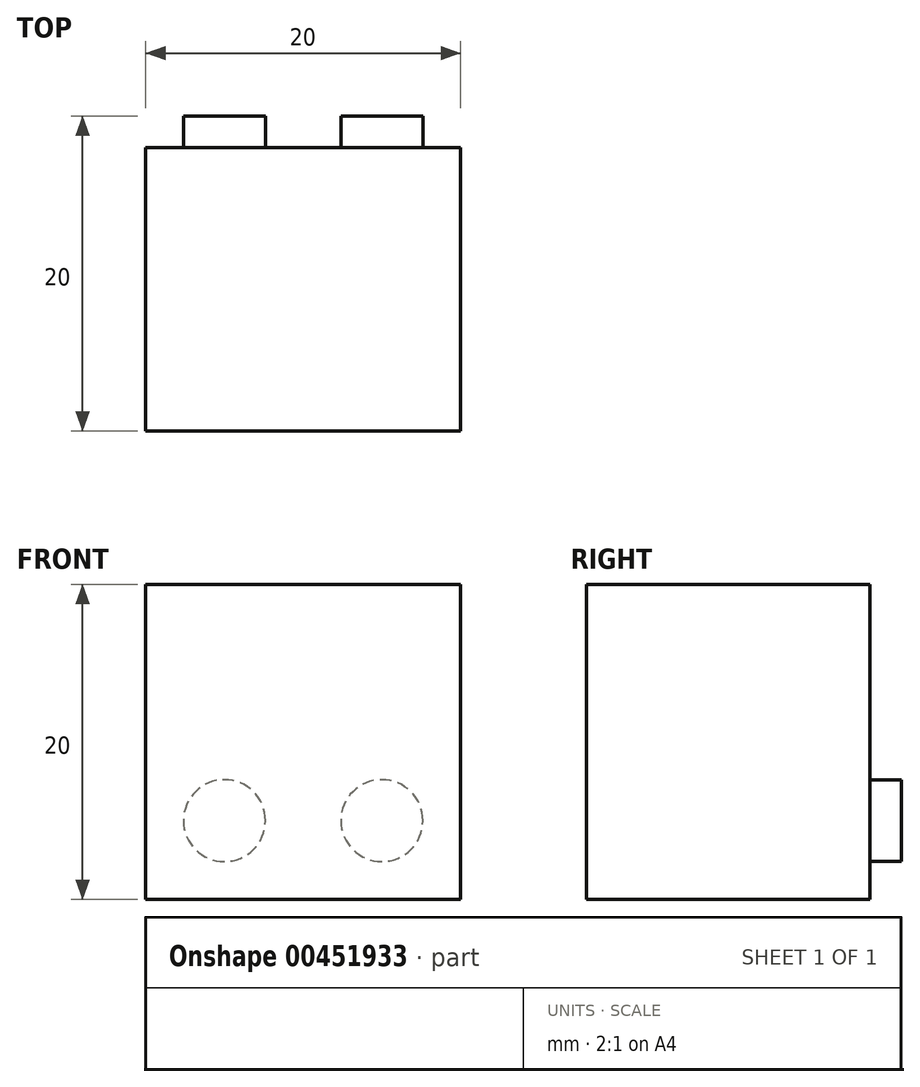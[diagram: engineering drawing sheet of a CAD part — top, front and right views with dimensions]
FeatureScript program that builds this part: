
annotation { "Feature Type Name" : "Feature", "Feature Type Description" : "" }
export const myFeature = defineFeature(function(context is Context, id is Id, definition is map)
    precondition{}
    {
        {
            var Q0;
            Q0=qCreatedBy(makeId("Front.planeOp"),FACE);
            var sketch = newSketch(context, id + "F0", { "sketchPlane" : qUnion([Q0])});
            skLineSegment(sketch, "E0.bottom", {"start": v(0, 0) * mm, "end": v(20, 0) * mm});
            skLineSegment(sketch, "E0.top", {"start": v(0, 20) * mm, "end": v(20, 20) * mm});
            skLineSegment(sketch, "E0.left", {"start": v(0, 0) * mm, "end": v(0, 20) * mm});
            skLineSegment(sketch, "E0.right", {"start": v(20, 0) * mm, "end": v(20, 20) * mm});
            skSolve(sketch);
        }
        {
            var Q0;
            Q0 = qSketchRegion(id + "F0", true);
            extrude(context, id + "F1", {"entities" : qUnion([Q0]), "depth" : 20 * mm});
        }
        {
            var Q0;
            Q0=makeQuery(id+"F1.opExtrude","CAP_FACE",FACE,{"disambiguationData":[OSD([sQuery(id+"F0.wireOp",EDGE,"E0.bottom"),sQuery(id+"F0.wireOp",EDGE,"E0.top"),sQuery(id+"F0.wireOp",EDGE,"E0.left"),sQuery(id+"F0.wireOp",EDGE,"E0.right")])],"isStart":true});
            var sketch = newSketch(context, id + "F2", { "sketchPlane" : qUnion([Q0])});
            skLineSegment(sketch, "E1", {"start": v(-20, 20) * mm, "end": v(0, 0) * mm, "construction": true});
            skLineSegment(sketch, "E2", {"start": v(0, 20) * mm, "end": v(-20, 0) * mm, "construction": true});
            skLineSegment(sketch, "E3", {"start": v(-10, 20) * mm, "end": v(-10, 0) * mm, "construction": true});
            skLineSegment(sketch, "E4", {"start": v(-20, 10) * mm, "end": v(0.43, 10) * mm, "construction": true});
            skCircle(sketch, "E5", {"center": v(-10, 10) * mm, "radius": 2.6 * mm});
            skCircle(sketch, "E6", {"center": v(-15, 15) * mm, "radius": 2.6 * mm});
            skCircle(sketch, "E7.MirrorC", {"center": v(-15, 5) * mm, "radius": 2.6 * mm});
            skLineSegment(sketch, "E8.MirrorCS", {"start": v(-20, 0) * mm, "end": v(0, 20) * mm, "construction": true});
            skCircle(sketch, "E9.MirrorC", {"center": v(-5, 15) * mm, "radius": 2.6 * mm});
            skCircle(sketch, "E10.MirrorC", {"center": v(-5, 5) * mm, "radius": 2.6 * mm});
            skSolve(sketch);
        }
        {
            var Q0;
            Q0=makeQuery(id+"F2.imprint","IMPRINT",FACE,{"disambiguationData":[TD([[makeQuery(id+"F2.imprint","IMPRINT",EDGE,{"derivedFrom":sQuery(id+"F2.wireOp",EDGE,"E5")}),-1.0]])]});
            var sketch = newSketch(context, id + "F3", { "sketchPlane" : qUnion([Q0])});
            skSolve(sketch);
        }
        {
            var Q0;
            Q0=makeQuery(id+"F3.imprint","IMPRINT",FACE,{"disambiguationData":[TD([[makeQuery(id+"F3.imprint","IMPRINT",EDGE,{"derivedFrom":makeQuery(id+"F2.imprint","IMPRINT",EDGE,{"derivedFrom":sQuery(id+"F2.wireOp",EDGE,"E7.MirrorC")})}),-1.0]])]});
            var sketch = newSketch(context, id + "F4", { "sketchPlane" : qUnion([Q0])});
            skSolve(sketch);
        }
        {
            var Q0;
            Q0=makeQuery(id+"F3.imprint","IMPRINT",FACE,{"disambiguationData":[TD([[makeQuery(id+"F3.imprint","IMPRINT",EDGE,{"derivedFrom":makeQuery(id+"F2.imprint","IMPRINT",EDGE,{"derivedFrom":sQuery(id+"F2.wireOp",EDGE,"E5")})}),-1.0]])]});
            var sketch = newSketch(context, id + "F5", { "sketchPlane" : qUnion([Q0])});
            skSolve(sketch);
        }
        {
            var Q0;
            Q0=makeQuery(id+"F3.imprint","IMPRINT",FACE,{"disambiguationData":[TD([[makeQuery(id+"F3.imprint","IMPRINT",EDGE,{"derivedFrom":makeQuery(id+"F2.imprint","IMPRINT",EDGE,{"derivedFrom":sQuery(id+"F2.wireOp",EDGE,"E5")})}),-1.0]])]});
            var Q1;
            Q1=makeQuery(id+"F3.imprint","IMPRINT",FACE,{"disambiguationData":[TD([[makeQuery(id+"F3.imprint","IMPRINT",EDGE,{"derivedFrom":makeQuery(id+"F2.imprint","IMPRINT",EDGE,{"derivedFrom":sQuery(id+"F2.wireOp",EDGE,"E9.MirrorC")})}),1.0]])]});
            extrude(context, id + "F6", {"entities" : qUnion([Q0, Q1]), "operationType" : NewBodyOperationType.REMOVE, "oppositeDirection" : true, "depth" : 1 * mm});
        }
        {
            var Q0;
            Q0=makeQuery(id+"F5.imprint","IMPRINT",FACE,{"disambiguationData":[TD([[makeQuery(id+"F5.imprint","IMPRINT",EDGE,{"derivedFrom":makeQuery(id+"F3.imprint","IMPRINT",EDGE,{"derivedFrom":makeQuery(id+"F2.imprint","IMPRINT",EDGE,{"derivedFrom":sQuery(id+"F2.wireOp",EDGE,"E5")})})}),-1.0]])]});
            var sketch = newSketch(context, id + "F7", { "sketchPlane" : qUnion([Q0])});
            skSolve(sketch);
        }
        {
            var Q0;
            Q0=makeQuery(id+"F5.imprint","IMPRINT",FACE,{"disambiguationData":[TD([[makeQuery(id+"F5.imprint","IMPRINT",EDGE,{"derivedFrom":makeQuery(id+"F3.imprint","IMPRINT",EDGE,{"derivedFrom":makeQuery(id+"F2.imprint","IMPRINT",EDGE,{"derivedFrom":sQuery(id+"F2.wireOp",EDGE,"E6")})})}),1.0]])]});
            var Q1;
            Q1=makeQuery(id+"F5.imprint","IMPRINT",FACE,{"disambiguationData":[TD([[makeQuery(id+"F5.imprint","IMPRINT",EDGE,{"derivedFrom":makeQuery(id+"F3.imprint","IMPRINT",EDGE,{"derivedFrom":makeQuery(id+"F2.imprint","IMPRINT",EDGE,{"derivedFrom":sQuery(id+"F2.wireOp",EDGE,"E9.MirrorC")})})}),1.0]])]});
            var Q2;
            Q2=makeQuery(id+"F5.imprint","IMPRINT",FACE,{"disambiguationData":[TD([[makeQuery(id+"F5.imprint","IMPRINT",EDGE,{"derivedFrom":makeQuery(id+"F3.imprint","IMPRINT",EDGE,{"derivedFrom":makeQuery(id+"F2.imprint","IMPRINT",EDGE,{"derivedFrom":sQuery(id+"F2.wireOp",EDGE,"E5")})})}),1.0]])]});
            var Q3;
            Q3=makeQuery(id+"F5.imprint","IMPRINT",FACE,{"disambiguationData":[TD([[makeQuery(id+"F5.imprint","IMPRINT",EDGE,{"derivedFrom":makeQuery(id+"F3.imprint","IMPRINT",EDGE,{"derivedFrom":makeQuery(id+"F2.imprint","IMPRINT",EDGE,{"derivedFrom":sQuery(id+"F2.wireOp",EDGE,"E10.MirrorC")})})}),-1.0]])]});
            var Q4;
            Q4=makeQuery(id+"F4.imprint","IMPRINT",FACE,{"disambiguationData":[TD([[makeQuery(id+"F4.imprint","IMPRINT",EDGE,{"derivedFrom":makeQuery(id+"F3.imprint","IMPRINT",EDGE,{"derivedFrom":makeQuery(id+"F2.imprint","IMPRINT",EDGE,{"derivedFrom":sQuery(id+"F2.wireOp",EDGE,"E7.MirrorC")})})}),-1.0]])]});
            extrude(context, id + "F8", {"entities" : qUnion([Q0, Q1, Q2, Q3, Q4]), "operationType" : NewBodyOperationType.REMOVE, "oppositeDirection" : true, "depth" : 2 * mm});
        }
    });
